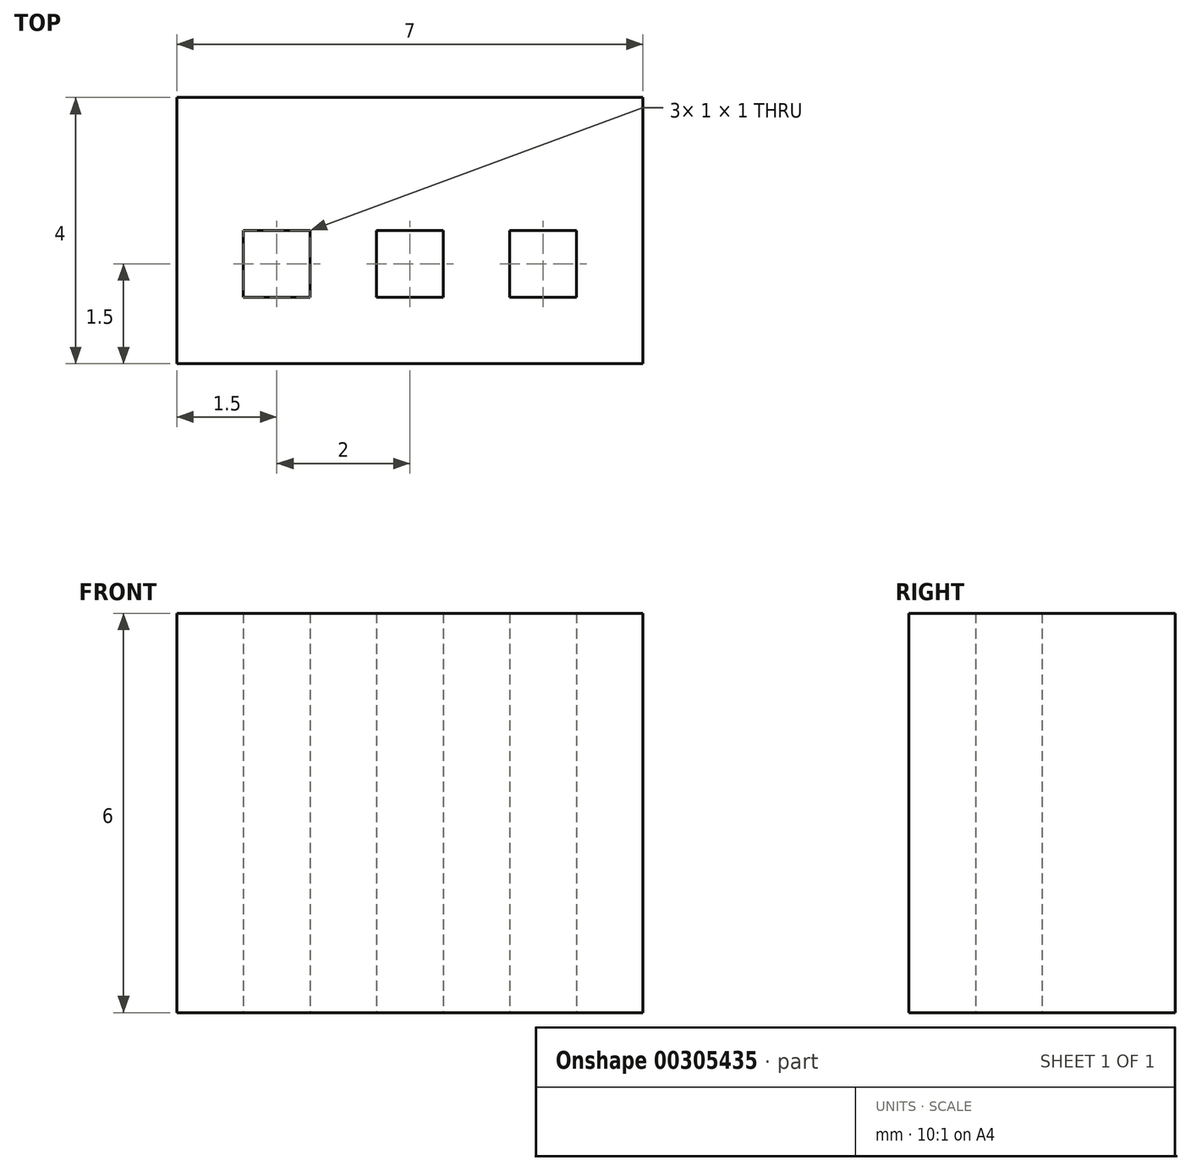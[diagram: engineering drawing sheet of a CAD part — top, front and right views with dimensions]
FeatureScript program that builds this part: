
annotation { "Feature Type Name" : "Feature", "Feature Type Description" : "" }
export const myFeature = defineFeature(function(context is Context, id is Id, definition is map)
    precondition{}
    {
        {
            var Q0;
            Q0=qCreatedBy(makeId("Top.planeOp"),FACE);
            var sketch = newSketch(context, id + "F0", { "sketchPlane" : qUnion([Q0])});
            skLineSegment(sketch, "E0.bottom", {"start": v(0, 0) * mm, "end": v(7, 0) * mm});
            skLineSegment(sketch, "E0.top", {"start": v(0, 4) * mm, "end": v(7, 4) * mm});
            skLineSegment(sketch, "E0.left", {"start": v(0, 0) * mm, "end": v(0, 4) * mm});
            skLineSegment(sketch, "E0.right", {"start": v(7, 0) * mm, "end": v(7, 4) * mm});
            skLineSegment(sketch, "E1", {"start": v(0, 0) * mm, "end": v(0, 1) * mm});
            skLineSegment(sketch, "E2", {"start": v(0, 1) * mm, "end": v(1, 1) * mm});
            skLineSegment(sketch, "E3", {"start": v(1, 1) * mm, "end": v(3, 1) * mm});
            skLineSegment(sketch, "E4", {"start": v(3, 1) * mm, "end": v(5, 1) * mm});
            skLineSegment(sketch, "E5.bottom", {"start": v(1, 1) * mm, "end": v(2, 1) * mm});
            skLineSegment(sketch, "E5.top", {"start": v(1, 2) * mm, "end": v(2, 2) * mm});
            skLineSegment(sketch, "E5.left", {"start": v(1, 1) * mm, "end": v(1, 2) * mm});
            skLineSegment(sketch, "E5.right", {"start": v(2, 1) * mm, "end": v(2, 2) * mm});
            skLineSegment(sketch, "E6.bottom", {"start": v(3, 1) * mm, "end": v(4, 1) * mm});
            skLineSegment(sketch, "E6.top", {"start": v(3, 2) * mm, "end": v(4, 2) * mm});
            skLineSegment(sketch, "E6.left", {"start": v(3, 1) * mm, "end": v(3, 2) * mm});
            skLineSegment(sketch, "E6.right", {"start": v(4, 1) * mm, "end": v(4, 2) * mm});
            skLineSegment(sketch, "E7.bottom", {"start": v(5, 1) * mm, "end": v(6, 1) * mm});
            skLineSegment(sketch, "E7.top", {"start": v(5, 2) * mm, "end": v(6, 2) * mm});
            skLineSegment(sketch, "E7.left", {"start": v(5, 1) * mm, "end": v(5, 2) * mm});
            skLineSegment(sketch, "E7.right", {"start": v(6, 1) * mm, "end": v(6, 2) * mm});
            skLineSegment(sketch, "E8", {"start": v(0, 0) * mm, "end": v(3, 0) * mm});
            skLineSegment(sketch, "E9.bottom", {"start": v(3, 0) * mm, "end": v(4, 0) * mm});
            skLineSegment(sketch, "E9.top", {"start": v(3, -1) * mm, "end": v(4, -1) * mm});
            skLineSegment(sketch, "E9.left", {"start": v(3, 0) * mm, "end": v(3, -1) * mm});
            skLineSegment(sketch, "E9.right", {"start": v(4, 0) * mm, "end": v(4, -1) * mm});
            skLineSegment(sketch, "E10", {"start": v(0, 0) * mm, "end": v(0, -1) * mm});
            skLineSegment(sketch, "E11", {"start": v(0, -1) * mm, "end": v(-1, -1) * mm});
            skLineSegment(sketch, "E12.bottom", {"start": v(-1, -1) * mm, "end": v(8, -1) * mm});
            skLineSegment(sketch, "E12.top", {"start": v(-1, 5) * mm, "end": v(8, 5) * mm});
            skLineSegment(sketch, "E12.left", {"start": v(-1, -1) * mm, "end": v(-1, 5) * mm});
            skLineSegment(sketch, "E12.right", {"start": v(8, -1) * mm, "end": v(8, 5) * mm});
            skSolve(sketch);
        }
        {
            var Q0;
            Q0=makeQuery(id+"F0.imprint","IMPRINT",FACE,{"disambiguationData":[TD([[makeQuery(id+"F0.imprint","IMPRINT",EDGE,{"derivedFrom":sQuery(id+"F0.wireOp",EDGE,"E0.bottom")}),1.0]])]});
            var Q1;
            Q1=makeQuery(id+"F0.imprint","IMPRINT",FACE,{"disambiguationData":[TD([[makeQuery(id+"F0.imprint","IMPRINT",EDGE,{"derivedFrom":sQuery(id+"F0.wireOp",EDGE,"E9.bottom")}),-1.0]])]});
            extrude(context, id + "F1", {"entities" : qUnion([Q0, Q1]), "depth" : 6 * mm});
        }
    });
